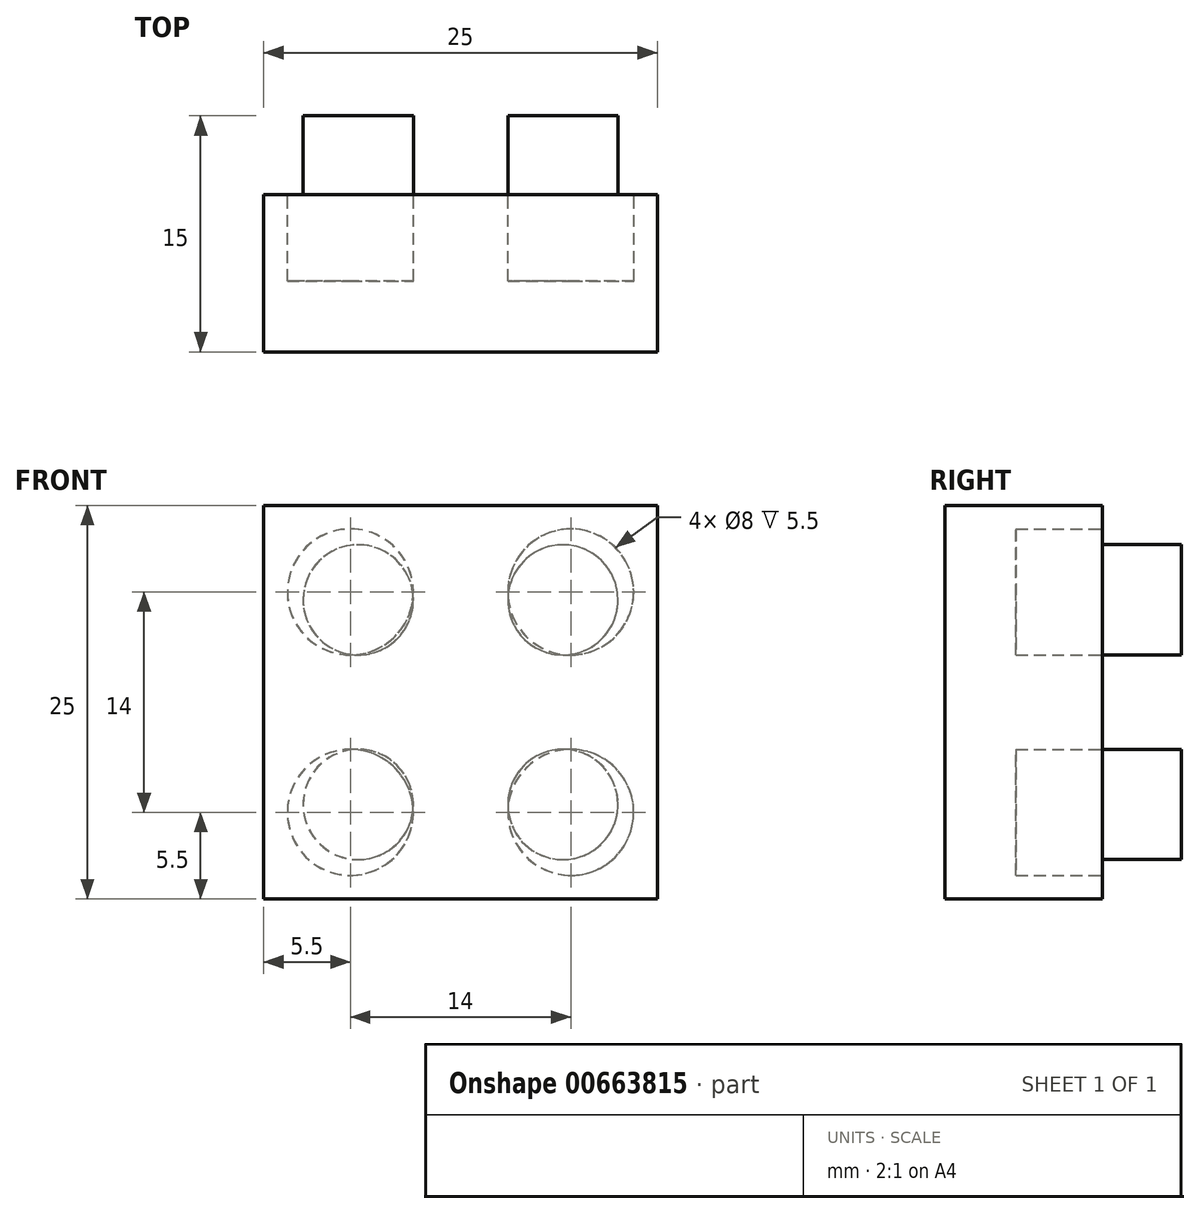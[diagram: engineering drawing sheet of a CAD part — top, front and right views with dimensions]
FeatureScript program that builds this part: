
annotation { "Feature Type Name" : "Feature", "Feature Type Description" : "" }
export const myFeature = defineFeature(function(context is Context, id is Id, definition is map)
    precondition{}
    {
        {
            var Q0;
            Q0=qCreatedBy(makeId("Front.planeOp"),FACE);
            var sketch = newSketch(context, id + "F0", { "sketchPlane" : qUnion([Q0])});
            skLineSegment(sketch, "E0.bottom", {"start": v(0, 0) * mm, "end": v(-25, 0) * mm});
            skLineSegment(sketch, "E0.top", {"start": v(0, 25) * mm, "end": v(-25, 25) * mm});
            skLineSegment(sketch, "E0.left", {"start": v(0, 0) * mm, "end": v(0, 25) * mm});
            skLineSegment(sketch, "E0.right", {"start": v(-25, 0) * mm, "end": v(-25, 25) * mm});
            skSolve(sketch);
        }
        {
            var Q0;
            Q0=makeQuery(id+"F0.imprint","IMPRINT",FACE,{"disambiguationData":[TD([[makeQuery(id+"F0.imprint","IMPRINT",EDGE,{"derivedFrom":sQuery(id+"F0.wireOp",EDGE,"E0.bottom")}),-1.0]])]});
            var Q1;
            Q1=sQuery(id+"F0.wireOp",EDGE,"E0.right");
            var Q2;
            Q2=sQuery(id+"F0.wireOp",EDGE,"E0.left");
            var Q3;
            Q3=sQuery(id+"F0.wireOp",EDGE,"E0.top");
            var Q4;
            Q4=sQuery(id+"F0.wireOp",EDGE,"E0.bottom");
            extrude(context, id + "F1", {"entities" : qUnion([Q0]), "surfaceEntities" : qUnion([Q1, Q2, Q3, Q4]), "depth" : 10 * mm, "offsetDistance" : 25.4 * mm});
        }
        {
            var Q0;
            Q0=qCreatedBy(makeId("Front.planeOp"),FACE);
            var sketch = newSketch(context, id + "F2", { "sketchPlane" : qUnion([Q0])});
            skCircle(sketch, "E1", {"center": v(-19, 19) * mm, "radius": 3.5 * mm});
            skCircle(sketch, "E2", {"center": v(-19, 6) * mm, "radius": 3.5 * mm});
            skCircle(sketch, "E3", {"center": v(-6, 6) * mm, "radius": 3.5 * mm});
            skCircle(sketch, "E4", {"center": v(-6, 19) * mm, "radius": 3.5 * mm});
            skSolve(sketch);
        }
        {
            var Q0;
            Q0 = qSketchRegion(id + "F2", true);
            extrude(context, id + "F3", {"entities" : qUnion([Q0]), "operationType" : NewBodyOperationType.ADD, "oppositeDirection" : true, "depth" : 5 * mm, "offsetDistance" : 25.4 * mm});
        }
        {
            var Q0;
            Q0=qCreatedBy(makeId("Front.planeOp"),FACE);
            var sketch = newSketch(context, id + "F4", { "sketchPlane" : qUnion([Q0])});
            skCircle(sketch, "E5", {"center": v(-19.5, 19.5) * mm, "radius": 4 * mm});
            skCircle(sketch, "E6", {"center": v(-19.5, 5.5) * mm, "radius": 4 * mm});
            skCircle(sketch, "E7", {"center": v(-5.5, 5.5) * mm, "radius": 4 * mm});
            skCircle(sketch, "E8", {"center": v(-5.5, 19.5) * mm, "radius": 4 * mm});
            skSolve(sketch);
        }
        {
            var Q0;
            Q0 = qSketchRegion(id + "F4", true);
            var Q1;
            Q1=makeQuery(id+"F1.opExtrude","CAP_FACE",FACE,{"disambiguationData":[OSD([sQuery(id+"F0.wireOp",EDGE,"E0.bottom"),sQuery(id+"F0.wireOp",EDGE,"E0.top"),sQuery(id+"F0.wireOp",EDGE,"E0.left"),sQuery(id+"F0.wireOp",EDGE,"E0.right")])],"isStart":false});
            extrude(context, id + "F5", {"entities" : qUnion([Q0, Q1]), "operationType" : NewBodyOperationType.REMOVE, "depth" : 5.5 * mm, "offsetDistance" : 25.4 * mm});
        }
    });
